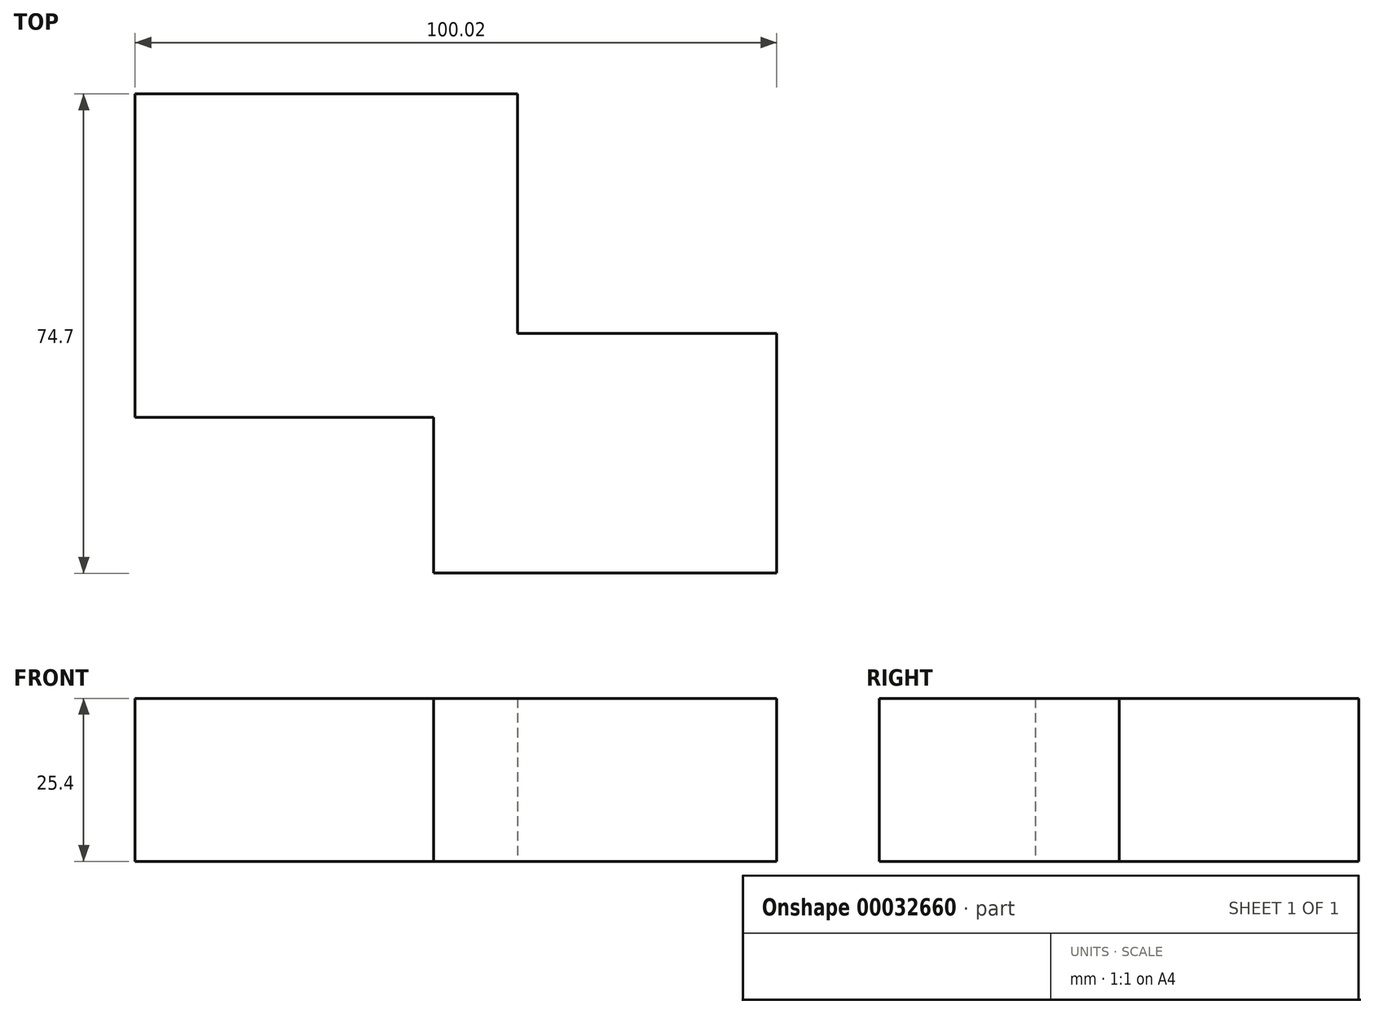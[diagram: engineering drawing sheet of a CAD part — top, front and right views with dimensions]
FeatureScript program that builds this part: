
annotation { "Feature Type Name" : "Feature", "Feature Type Description" : "" }
export const myFeature = defineFeature(function(context is Context, id is Id, definition is map)
    precondition{}
    {
        {
            var Q0;
            Q0=qCreatedBy(makeId("Top.planeOp"),FACE);
            var sketch = newSketch(context, id + "F0", { "sketchPlane" : qUnion([Q0])});
            skLineSegment(sketch, "E0.bottom", {"start": v(-38.37, 28.78) * mm, "end": v(21.23, 28.78) * mm});
            skLineSegment(sketch, "E0.top", {"start": v(-38.37, -21.62) * mm, "end": v(21.23, -21.62) * mm});
            skLineSegment(sketch, "E0.left", {"start": v(-38.37, 28.78) * mm, "end": v(-38.37, -21.62) * mm});
            skLineSegment(sketch, "E0.right", {"start": v(21.23, 28.78) * mm, "end": v(21.23, -21.62) * mm});
            skLineSegment(sketch, "E1.bottom", {"start": v(8.19, -8.57) * mm, "end": v(61.65, -8.57) * mm});
            skLineSegment(sketch, "E1.top", {"start": v(8.19, -45.92) * mm, "end": v(61.65, -45.92) * mm});
            skLineSegment(sketch, "E1.left", {"start": v(8.19, -8.57) * mm, "end": v(8.19, -45.92) * mm});
            skLineSegment(sketch, "E1.right", {"start": v(61.65, -8.57) * mm, "end": v(61.65, -45.92) * mm});
            skSolve(sketch);
        }
        {
            var Q0;
            Q0 = qSketchRegion(id + "F0", true);
            extrude(context, id + "F1", {"entities" : qUnion([Q0]), "depth" : 25.4 * mm});
        }
    });
